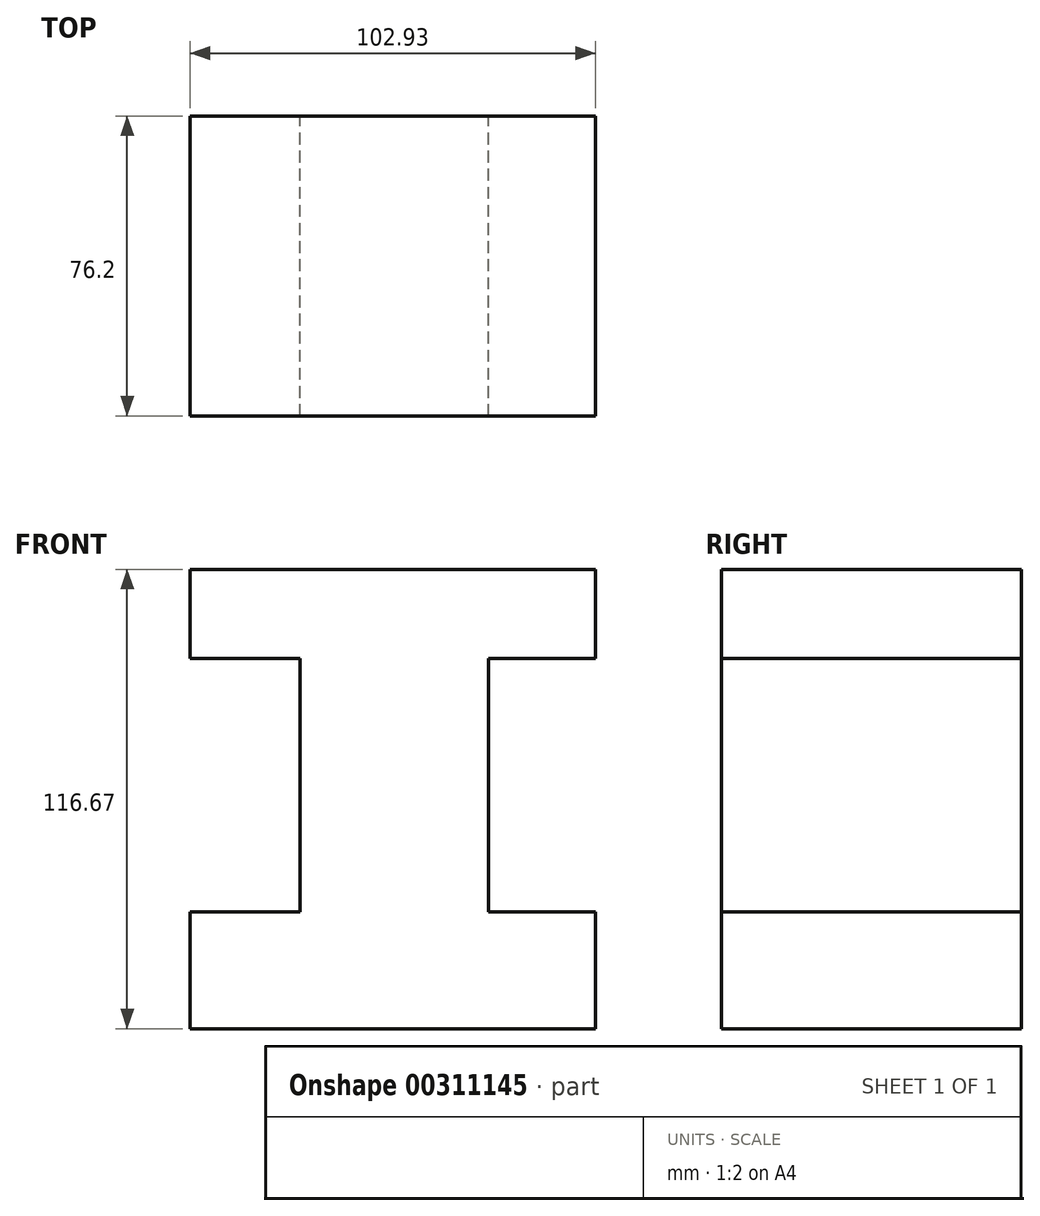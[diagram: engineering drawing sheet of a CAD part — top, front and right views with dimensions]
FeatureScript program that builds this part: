
annotation { "Feature Type Name" : "Feature", "Feature Type Description" : "" }
export const myFeature = defineFeature(function(context is Context, id is Id, definition is map)
    precondition{}
    {
        {
            var Q0;
            Q0=qCreatedBy(makeId("Front.planeOp"),FACE);
            var sketch = newSketch(context, id + "F0", { "sketchPlane" : qUnion([Q0])});
            skLineSegment(sketch, "E0", {"start": v(-50.8, -45.16) * mm, "end": v(52.13, -45.16) * mm});
            skLineSegment(sketch, "E1", {"start": v(52.13, -45.16) * mm, "end": v(52.13, -15.55) * mm});
            skLineSegment(sketch, "E2", {"start": v(52.13, -15.55) * mm, "end": v(24.99, -15.55) * mm});
            skLineSegment(sketch, "E3", {"start": v(24.99, -15.55) * mm, "end": v(24.99, 48.95) * mm});
            skLineSegment(sketch, "E4", {"start": v(24.99, 48.95) * mm, "end": v(52.13, 48.95) * mm});
            skLineSegment(sketch, "E5", {"start": v(52.13, 48.95) * mm, "end": v(52.13, 71.51) * mm});
            skLineSegment(sketch, "E6", {"start": v(52.13, 71.51) * mm, "end": v(-50.8, 71.51) * mm});
            skLineSegment(sketch, "E7", {"start": v(-50.8, 71.51) * mm, "end": v(-50.8, 48.95) * mm});
            skLineSegment(sketch, "E8", {"start": v(-50.8, 48.95) * mm, "end": v(-22.95, 48.95) * mm});
            skLineSegment(sketch, "E9", {"start": v(-22.95, 48.95) * mm, "end": v(-22.95, -15.55) * mm});
            skLineSegment(sketch, "E10", {"start": v(-22.95, -15.55) * mm, "end": v(-50.8, -15.55) * mm});
            skLineSegment(sketch, "E11", {"start": v(-50.8, -15.55) * mm, "end": v(-50.8, -45.16) * mm});
            skSolve(sketch);
        }
        {
            var Q0;
            Q0=makeQuery(id+"F0.imprint","IMPRINT",FACE,{"disambiguationData":[TD([[makeQuery(id+"F0.imprint","IMPRINT",EDGE,{"derivedFrom":sQuery(id+"F0.wireOp",EDGE,"E0")}),1.0]])]});
            extrude(context, id + "F1", {"entities" : qUnion([Q0]), "depth" : 76.2 * mm});
        }
    });
